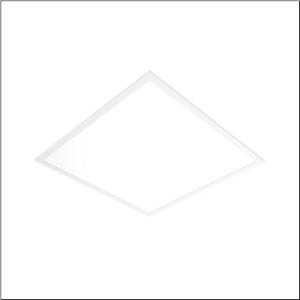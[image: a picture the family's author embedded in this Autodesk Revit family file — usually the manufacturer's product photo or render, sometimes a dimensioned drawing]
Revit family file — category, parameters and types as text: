
# Revit family: apollon_41_51mh11wd2m43
name_source: partatom
category: Lighting Fixtures
units: mm (PartAtom-declared; Revit-internal decimal feet)

## family parameters
Cut with Voids When Loaded = No
Host = Face
Light Source = No
Part Type = Normal
Room Calculation Point = No
Round Connector Dimension = Use Diameter
Shared = No

## types (1)
- --- (1 x LED, 530 lm, 4.9 W, 4000K)
    Apparent Load = 5 VA
    CIE Flux Codes = 61 87 97 100 100
    Color Rendering = 80
    Color Temperature = 4000K
    Default Elevation = 1800 mm
    Description = Apollon 41, office luminaire, primary optical cover: prismatic diffuser, of PS, light emission: direct distribution, primary light characteristic: symmetric, installation type: lay-in mounting, LED, rated luminous flux: 3.500lm, luminous efficacy: 123lm/W, light colour: 830/840, colour temperature: 3000/4000K, control gear: DALI 2, with terminal, 5-pole, mains connection: 220..240V, AC/DC, 0/50..60Hz, suitable for self-contained emergency lighting element 58DB00B013A with integrated self-test function according to EN 60598-2-22, housing, of aluminium section, traffic white (RAL 9016), module: M625, length: 620mm, width: 620mm, height: 60mm, recess depth: 180mm, housing upper side, of sheet steel, protection rating (complete): IP20, protection rating (lamp compartment, on room side): IP40, insulation class (complete): insulation class II (safety insulation), certification: CE, ENEC, impact resistance: IK03, permissible operating ambient temperature: -25..+40°C, packaging unit: 1 piece
    Height = 0 mm  [stored 0 ft]
    Lamp = 1 x LED
    Lamp Light Flux = 530 lm
    Lamp Power = 4.9 W
    Lamp count = 1
    Length = 620 mm
    Luminous efficacy = 108 lm/W
    Manufacturer = Siteco
    ModVariant = No
    Model = 51MH11WD2M43
    Mounting Place = Ceiling
    Mounting Type = Recessed
    Number of Poles = 1
    OnlyDefault = Yes
    Power Factor = 1
    Product Name = Apollon 41
    Product group = office luminaire | ceiling recessed
    ProductGroupID = 400
    Protection Class = Protection class II
    Protection Degree = IP 20
    RLX_Detail_Level = 1
    RLX_Emergency_Light_Flux = 0 lm
    RLX_Emergency_Type = 0
    RLX_Emergency_Type_DB = No
    RlxData = <blob elided: 12921 chars, md5=9ed0d747>
    Socket = socket
    Standby Power = 0 W
    System Light Flux = 530 lm
    System Power = 5 W
    Type Comments = : DC mode (central or group accumulator) initial emergency light level
    Type Image = l_1291024.jpg
    URL = http://relux.com
    VarID = @adj_000007
    Voltage = 0 V
    Weight = 0.00 kg
    Width = 620 mm

note: [stored X ft] marks values corroborated as IEEE doubles in the binary element streams (Revit-internal decimal feet)

## geometry (parser evidence)
native form markers: Sweep x8
no freeform markers — native parametric forms only
